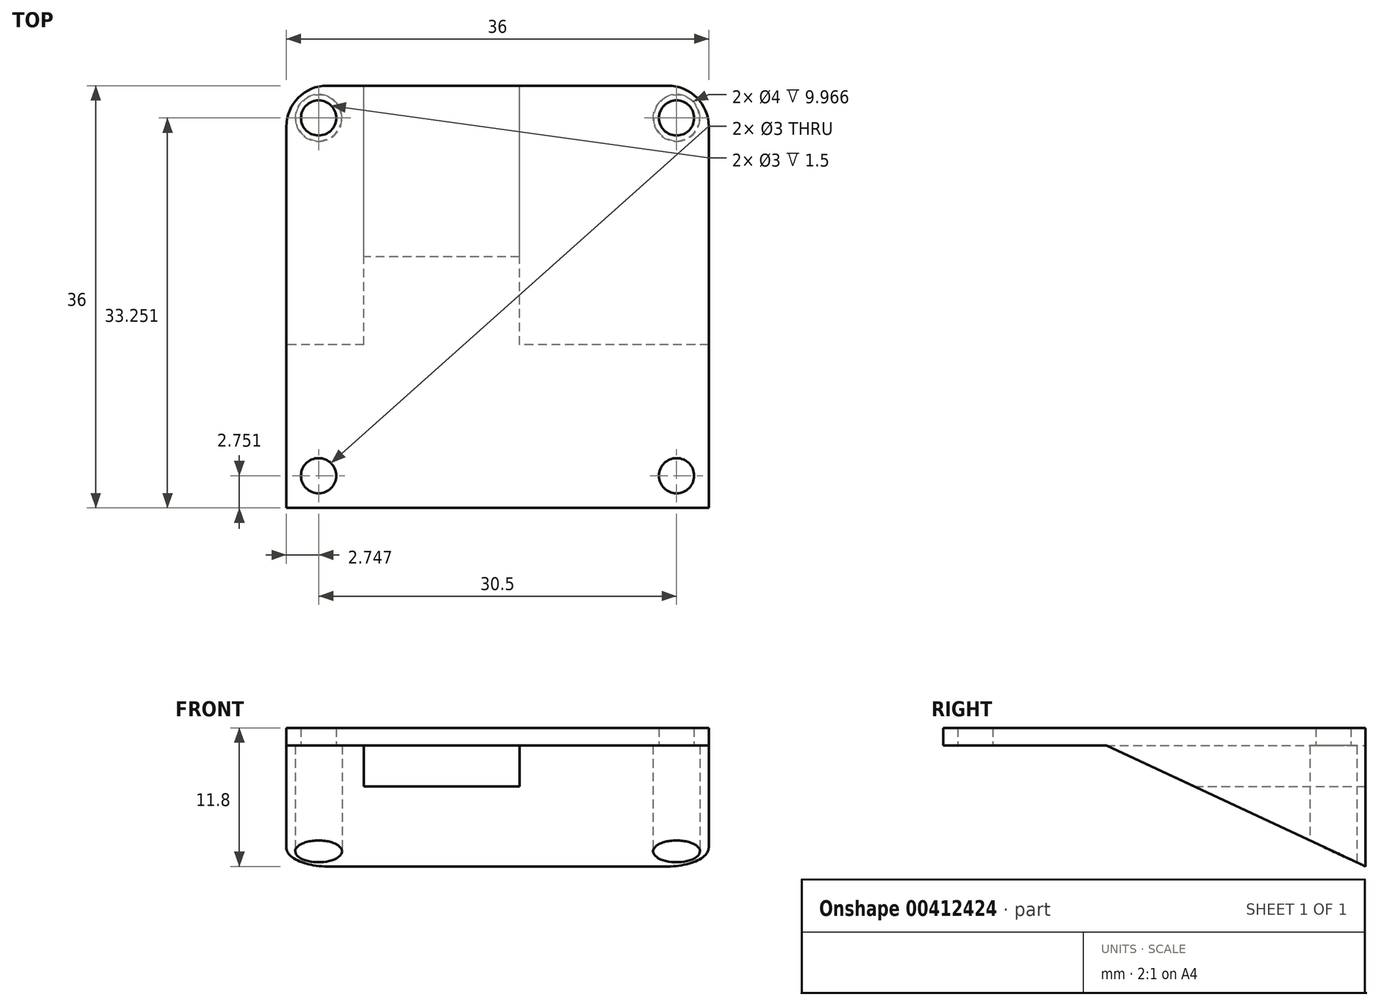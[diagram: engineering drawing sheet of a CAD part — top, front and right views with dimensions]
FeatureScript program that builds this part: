
annotation { "Feature Type Name" : "Feature", "Feature Type Description" : "" }
export const myFeature = defineFeature(function(context is Context, id is Id, definition is map)
    precondition{}
    {
        {
            var Q0;
            Q0=qCreatedBy(makeId("Top.planeOp"),FACE);
            var sketch = newSketch(context, id + "F0", { "sketchPlane" : qUnion([Q0])});
            skLineSegment(sketch, "E0.bottom", {"start": v(-5.46, -6) * mm, "end": v(30.54, -6) * mm});
            skLineSegment(sketch, "E0.top", {"start": v(-5.46, -42) * mm, "end": v(30.54, -42) * mm});
            skLineSegment(sketch, "E0.left", {"start": v(-5.46, -6) * mm, "end": v(-5.46, -42) * mm});
            skLineSegment(sketch, "E0.right", {"start": v(30.54, -6) * mm, "end": v(30.54, -42) * mm});
            skLineSegment(sketch, "E1.bottom", {"start": v(-5.46, -6) * mm, "end": v(-4.01, -6) * mm});
            skLineSegment(sketch, "E1.left", {"start": v(-5.46, -6) * mm, "end": v(-5.46, -11.1) * mm});
            skLineSegment(sketch, "E2.bottom", {"start": v(-5.46, -42) * mm, "end": v(-4.01, -42) * mm});
            skLineSegment(sketch, "E2.left", {"start": v(-5.46, -42) * mm, "end": v(-5.46, -36.9) * mm});
            skLineSegment(sketch, "E3.bottom", {"start": v(30.54, -42) * mm, "end": v(29.09, -42) * mm});
            skLineSegment(sketch, "E3.left", {"start": v(30.54, -42) * mm, "end": v(30.54, -36.9) * mm});
            skLineSegment(sketch, "E4.bottom", {"start": v(30.54, -6) * mm, "end": v(29.09, -6) * mm});
            skLineSegment(sketch, "E4.left", {"start": v(30.54, -6) * mm, "end": v(30.54, -11.1) * mm});
            skLineSegment(sketch, "E5", {"start": v(-5.46, -24) * mm, "end": v(30.54, -24) * mm, "construction": true});
            skLineSegment(sketch, "E6", {"start": v(12.54, -6) * mm, "end": v(12.54, -42) * mm, "construction": true});
            skLineSegment(sketch, "E7.bottom", {"start": v(-2.71, -39.25) * mm, "end": v(27.79, -39.25) * mm, "construction": true});
            skLineSegment(sketch, "E7.top", {"start": v(-2.71, -8.75) * mm, "end": v(27.79, -8.75) * mm, "construction": true});
            skLineSegment(sketch, "E7.left", {"start": v(-2.71, -39.25) * mm, "end": v(-2.71, -8.75) * mm, "construction": true});
            skLineSegment(sketch, "E7.right", {"start": v(27.79, -39.25) * mm, "end": v(27.79, -8.75) * mm, "construction": true});
            skPoint(sketch, "E7.middle", {"position": v(12.54, -24) * mm});
            skCircle(sketch, "E8", {"center": v(27.79, -8.75) * mm, "radius": 1.5 * mm});
            skCircle(sketch, "E9", {"center": v(-2.71, -8.75) * mm, "radius": 1.5 * mm});
            skCircle(sketch, "E10", {"center": v(-2.71, -39.25) * mm, "radius": 1.5 * mm});
            skCircle(sketch, "E11", {"center": v(27.79, -39.25) * mm, "radius": 1.5 * mm});
            skCircle(sketch, "E12", {"center": v(27.79, -8.75) * mm, "radius": 2 * mm});
            skCircle(sketch, "E13", {"center": v(-2.71, -8.75) * mm, "radius": 2 * mm});
            skSolve(sketch);
        }
        {
            var Q0;
            Q0=makeQuery(id+"F0.imprint","IMPRINT",FACE,{"disambiguationData":[TD([[makeQuery(id+"F0.imprint","IMPRINT",EDGE,{"derivedFrom":sQuery(id+"F0.wireOp",EDGE,"E0.bottom")}),-1.0]])]});
            extrude(context, id + "F1", {"entities" : qUnion([Q0]), "depth" : 1.5 * mm, "offsetDistance" : 25 * mm});
        }
        {
            var Q0;
            Q0=makeQuery(id+"FM9TktC3HsfJw4X_1.boolean.opBoolean","MERGE",FACE,{"derivedFrom":[makeQuery(id+"F1.opExtrude","SWEPT_FACE",FACE,{"disambiguationData":[OSD([sQuery(id+"F0.wireOp",EDGE,"E0.left")])]}),makeQuery(id+"FM9TktC3HsfJw4X_1.opExtrude","SWEPT_FACE",FACE,{"disambiguationData":[OSD([sQuery(id+"F0.wireOp",EDGE,"E1.left")])]}),makeQuery(id+"FM9TktC3HsfJw4X_1.opExtrude","SWEPT_FACE",FACE,{"disambiguationData":[OSD([sQuery(id+"F0.wireOp",EDGE,"E2.left")])]})]});
            var sketch = newSketch(context, id + "F2", { "sketchPlane" : qUnion([Q0])});
            skLineSegment(sketch, "E14", {"start": v(6, 0) * mm, "end": v(6, -10.3) * mm});
            skLineSegment(sketch, "E15", {"start": v(6, 0) * mm, "end": v(28.1, 0) * mm});
            skLineSegment(sketch, "E16", {"start": v(28.1, 0) * mm, "end": v(6, -10.3) * mm});
            skSolve(sketch);
        }
        {
            var Q0;
            Q0=makeQuery(id+"F2.imprint","IMPRINT",FACE,{"disambiguationData":[TD([[makeQuery(id+"F2.imprint","IMPRINT",EDGE,{"derivedFrom":sQuery(id+"F2.wireOp",EDGE,"E14")}),1.0]])]});
            extrude(context, id + "F3", {"entities" : qUnion([Q0]), "operationType" : NewBodyOperationType.ADD, "oppositeDirection" : true, "depth" : 36 * mm, "offsetDistance" : 25 * mm});
        }
        {
            var Q0;
            Q0=makeQuery(id+"F3.boolean.opBoolean","MERGE",FACE,{"derivedFrom":[makeQuery(id+"FM9TktC3HsfJw4X_1.boolean.opBoolean","MERGE",FACE,{"derivedFrom":[makeQuery(id+"F1.opExtrude","SWEPT_FACE",FACE,{"disambiguationData":[OSD([sQuery(id+"F0.wireOp",EDGE,"E0.bottom")])]}),makeQuery(id+"FM9TktC3HsfJw4X_1.opExtrude","SWEPT_FACE",FACE,{"disambiguationData":[OSD([sQuery(id+"F0.wireOp",EDGE,"E1.bottom")])]}),makeQuery(id+"FM9TktC3HsfJw4X_1.opExtrude","SWEPT_FACE",FACE,{"disambiguationData":[OSD([sQuery(id+"F0.wireOp",EDGE,"E4.bottom")])]})]}),makeQuery(id+"F3.opExtrude","SWEPT_FACE",FACE,{"disambiguationData":[OSD([sQuery(id+"F2.wireOp",EDGE,"E14")])]})]});
            var sketch = newSketch(context, id + "F4", { "sketchPlane" : qUnion([Q0])});
            skLineSegment(sketch, "E17", {"start": v(-30.54, 0) * mm, "end": v(-14.4, 0) * mm});
            skLineSegment(sketch, "E18.bottom", {"start": v(-14.4, 0) * mm, "end": v(-1.15, 0) * mm});
            skLineSegment(sketch, "E18.top", {"start": v(-14.4, -3.5) * mm, "end": v(-1.15, -3.5) * mm});
            skLineSegment(sketch, "E18.left", {"start": v(-14.4, 0) * mm, "end": v(-14.4, -3.5) * mm});
            skLineSegment(sketch, "E18.right", {"start": v(-1.15, 0) * mm, "end": v(-1.15, -3.5) * mm});
            skSolve(sketch);
        }
        {
            var Q0;
            Q0=makeQuery(id+"F4.imprint","IMPRINT",FACE,{"disambiguationData":[TD([[makeQuery(id+"F4.imprint","IMPRINT",EDGE,{"derivedFrom":sQuery(id+"F4.wireOp",EDGE,"E18.bottom")}),-1.0]])]});
            extrude(context, id + "F5", {"entities" : qUnion([Q0]), "operationType" : NewBodyOperationType.REMOVE, "oppositeDirection" : true, "depth" : 25 * mm});
        }
        {
            var Q0;
            Q0=makeQuery(id+"F0.imprint","IMPRINT",FACE,{"disambiguationData":[TD([[makeQuery(id+"F0.imprint","IMPRINT",EDGE,{"derivedFrom":sQuery(id+"F0.wireOp",EDGE,"E8")}),-1.0]])]});
            var Q1;
            Q1=makeQuery(id+"F0.imprint","IMPRINT",FACE,{"disambiguationData":[TD([[makeQuery(id+"F0.imprint","IMPRINT",EDGE,{"derivedFrom":sQuery(id+"F0.wireOp",EDGE,"E9")}),-1.0]])]});
            var Q2;
            Q2=makeQuery(id+"F0.imprint","IMPRINT",FACE,{"disambiguationData":[TD([[makeQuery(id+"F0.imprint","IMPRINT",EDGE,{"derivedFrom":sQuery(id+"F0.wireOp",EDGE,"E9")}),1.0]])]});
            var Q3;
            Q3=makeQuery(id+"F0.imprint","IMPRINT",FACE,{"disambiguationData":[TD([[makeQuery(id+"F0.imprint","IMPRINT",EDGE,{"derivedFrom":sQuery(id+"F0.wireOp",EDGE,"E8")}),1.0]])]});
            extrude(context, id + "F6", {"entities" : qUnion([Q0, Q1, Q2, Q3]), "operationType" : NewBodyOperationType.REMOVE, "oppositeDirection" : true, "depth" : 25 * mm, "offsetDistance" : 25 * mm});
        }
        {
            var Q0;
            Q0=makeQuery(id+"F0.imprint","IMPRINT",FACE,{"disambiguationData":[TD([[makeQuery(id+"F0.imprint","IMPRINT",EDGE,{"derivedFrom":sQuery(id+"F0.wireOp",EDGE,"E8")}),-1.0]])]});
            var Q1;
            Q1=makeQuery(id+"F0.imprint","IMPRINT",FACE,{"disambiguationData":[TD([[makeQuery(id+"F0.imprint","IMPRINT",EDGE,{"derivedFrom":sQuery(id+"F0.wireOp",EDGE,"E9")}),-1.0]])]});
            extrude(context, id + "F7", {"entities" : qUnion([Q0, Q1]), "operationType" : NewBodyOperationType.ADD, "depth" : 1.5 * mm, "offsetDistance" : 25 * mm});
        }
        {
            var Q0;
            Q0=makeQuery(id+"F3.boolean.opBoolean","MERGE",EDGE,{"derivedFrom":[makeQuery(id+"F1.opExtrude","SWEPT_EDGE",EDGE,{"disambiguationData":[OSD([sQuery(id+"F0.wireOp",EDGE,"E1.bottom"),sQuery(id+"F0.wireOp",EDGE,"E1.left")])]}),makeQuery(id+"F3.opExtrude","CAP_EDGE",EDGE,{"disambiguationData":[OSD([sQuery(id+"F2.wireOp",EDGE,"E14")])],"isStart":true})]});
            var Q1;
            Q1=makeQuery(id+"F1.opExtrude","SWEPT_EDGE",EDGE,{"disambiguationData":[OSD([sQuery(id+"F0.wireOp",EDGE,"E2.bottom"),sQuery(id+"F0.wireOp",EDGE,"E2.left")])]});
            var Q2;
            Q2=makeQuery(id+"F3.boolean.opBoolean","MERGE",EDGE,{"derivedFrom":[makeQuery(id+"F1.opExtrude","SWEPT_EDGE",EDGE,{"disambiguationData":[OSD([sQuery(id+"F0.wireOp",EDGE,"E4.bottom"),sQuery(id+"F0.wireOp",EDGE,"E4.left")])]}),makeQuery(id+"F3.opExtrude","CAP_EDGE",EDGE,{"disambiguationData":[OSD([sQuery(id+"F2.wireOp",EDGE,"E14")])],"isStart":false})]});
            var Q3;
            Q3=makeQuery(id+"F1.opExtrude","SWEPT_EDGE",EDGE,{"disambiguationData":[OSD([sQuery(id+"F0.wireOp",EDGE,"E3.bottom"),sQuery(id+"F0.wireOp",EDGE,"E3.left")])]});
            fillet(context, id + "F8", {"entities" : qUnion([Q0, Q1, Q2, Q3]), "radius" : 3.5 * mm, "tangentPropagation" : true, "allowEdgeOverflow" : false});
        }
    });
